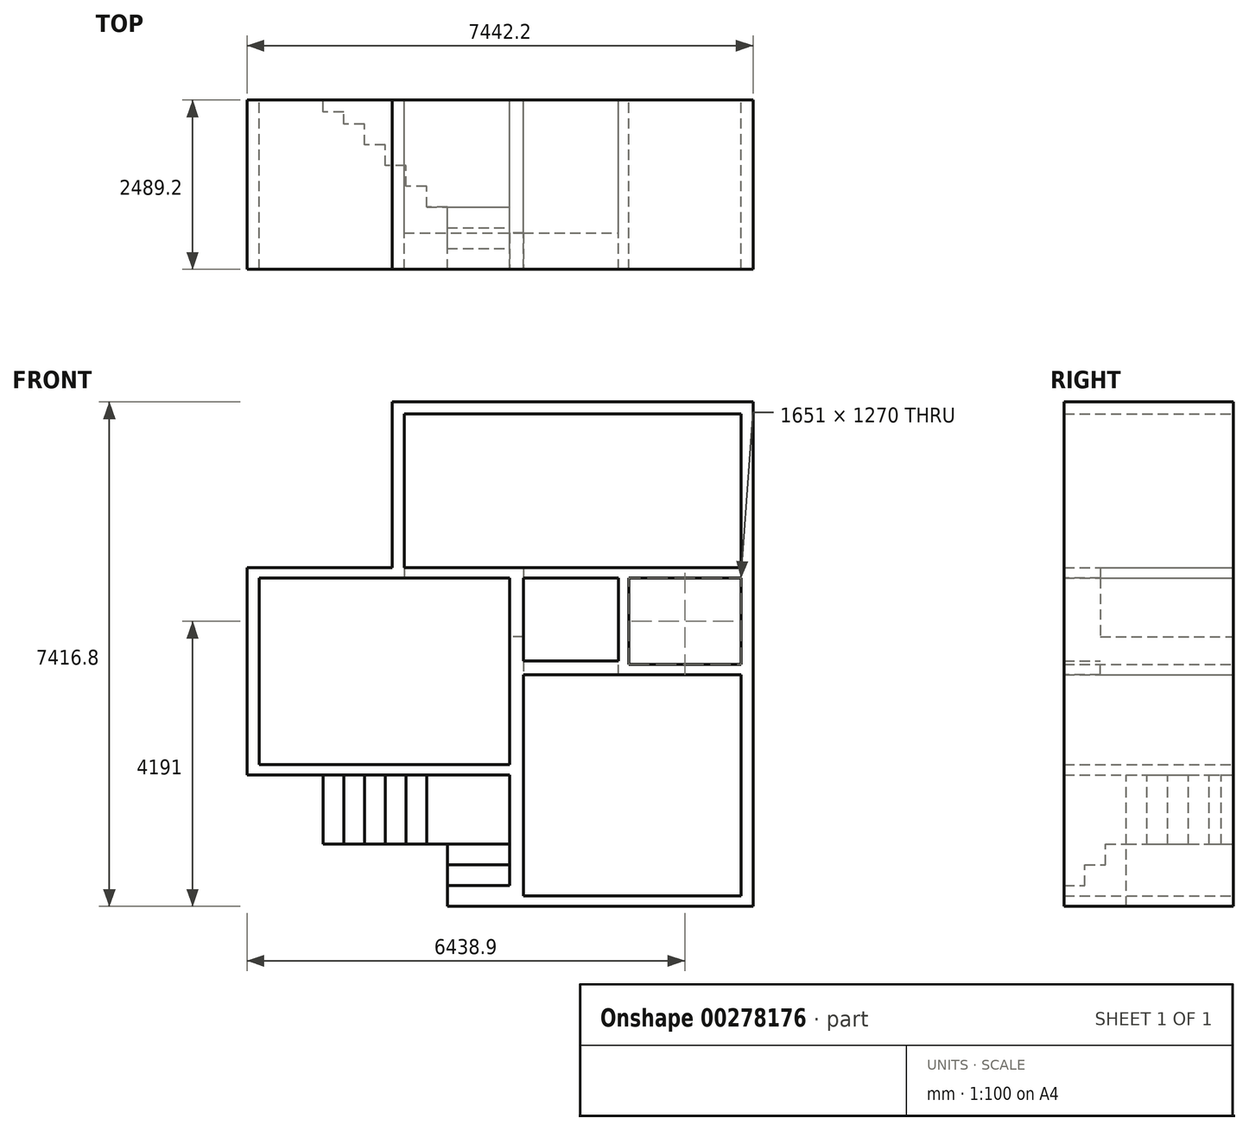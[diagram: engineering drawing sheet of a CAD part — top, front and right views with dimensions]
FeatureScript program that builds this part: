
annotation { "Feature Type Name" : "Feature", "Feature Type Description" : "" }
export const myFeature = defineFeature(function(context is Context, id is Id, definition is map)
    precondition{}
    {
        {
            var Q0;
            Q0=qCreatedBy(makeId("Front.planeOp"),FACE);
            var sketch = newSketch(context, id + "F0", { "sketchPlane" : qUnion([Q0])});
            skLineSegment(sketch, "E0", {"start": v(4953, 0) * mm, "end": v(4953, 2260.6) * mm});
            skLineSegment(sketch, "E1", {"start": v(4953, 2260.6) * mm, "end": v(0, 2260.6) * mm});
            skLineSegment(sketch, "E2", {"start": v(0, 2260.6) * mm, "end": v(0, 0) * mm});
            skLineSegment(sketch, "E3", {"start": v(4953, -1574.8) * mm, "end": v(3149.6, -1574.8) * mm});
            skLineSegment(sketch, "E4", {"start": v(3149.6, -1574.8) * mm, "end": v(3149.6, -152.4) * mm});
            skLineSegment(sketch, "E5", {"start": v(3302, -152.4) * mm, "end": v(3302, -1422.4) * mm});
            skLineSegment(sketch, "E6", {"start": v(3302, -1422.4) * mm, "end": v(4953, -1422.4) * mm});
            skLineSegment(sketch, "E7", {"start": v(4953, -1422.4) * mm, "end": v(4953, -152.4) * mm});
            skLineSegment(sketch, "E8", {"start": v(3302, -152.4) * mm, "end": v(4953, -152.4) * mm});
            skLineSegment(sketch, "E9", {"start": v(5130.8, 2438.4) * mm, "end": v(-177.8, 2438.4) * mm});
            skLineSegment(sketch, "E10", {"start": v(-177.8, 2438.4) * mm, "end": v(-177.8, 0) * mm});
            skLineSegment(sketch, "E11", {"start": v(-177.8, 0) * mm, "end": v(-2311.4, 0) * mm});
            skLineSegment(sketch, "E12", {"start": v(5130.8, 2438.4) * mm, "end": v(5130.8, -4978.4) * mm});
            skLineSegment(sketch, "E13", {"start": v(-2133.6, -152.4) * mm, "end": v(-2133.6, -2895.6) * mm});
            skLineSegment(sketch, "E14", {"start": v(-2133.6, -2895.6) * mm, "end": v(1549.4, -2895.6) * mm});
            skLineSegment(sketch, "E15", {"start": v(-2311.4, -3048) * mm, "end": v(1549.4, -3048) * mm});
            skLineSegment(sketch, "E16", {"start": v(1549.4, -3048) * mm, "end": v(1549.4, -4978.4) * mm});
            skLineSegment(sketch, "E17", {"start": v(1752.6, -4826) * mm, "end": v(4978.4, -4826) * mm});
            skLineSegment(sketch, "E18", {"start": v(1549.4, -4978.4) * mm, "end": v(5130.8, -4978.4) * mm});
            skLineSegment(sketch, "E19", {"start": v(4953, -4826) * mm, "end": v(4953, -1574.8) * mm});
            skLineSegment(sketch, "E20", {"start": v(1752.6, -1016) * mm, "end": v(1752.6, -4826) * mm});
            skLineSegment(sketch, "E21", {"start": v(-2133.6, -152.4) * mm, "end": v(0, -152.4) * mm});
            skLineSegment(sketch, "E22", {"start": v(0, -152.4) * mm, "end": v(0, 0) * mm});
            skLineSegment(sketch, "E23", {"start": v(1549.4, -2895.6) * mm, "end": v(1549.4, -1016) * mm});
            skLineSegment(sketch, "E24", {"start": v(1549.4, -1016) * mm, "end": v(1752.6, -1016) * mm});
            skLineSegment(sketch, "E25", {"start": v(3149.6, -152.4) * mm, "end": v(1752.6, -152.4) * mm});
            skLineSegment(sketch, "E26", {"start": v(1752.6, -152.4) * mm, "end": v(1752.6, 0) * mm});
            skLineSegment(sketch, "E27", {"start": v(1752.6, 0) * mm, "end": v(4953, 0) * mm});
            skLineSegment(sketch, "E28", {"start": v(-2311.4, -3048) * mm, "end": v(-2311.4, 0) * mm});
            skSolve(sketch);
        }
        {
            var Q0;
            Q0 = qSketchRegion(id + "F0", true);
            extrude(context, id + "F1", {"entities" : qUnion([Q0]), "depth" : 2489.2 * mm});
        }
        {
            var Q0;
            Q0=makeQuery(id+"F1.opExtrude","SWEPT_FACE",FACE,{"disambiguationData":[OSD([sQuery(id+"F0.wireOp",EDGE,"E26")])]});
            var sketch = newSketch(context, id + "F2", { "sketchPlane" : qUnion([Q0])});
            skLineSegment(sketch, "E29.bottom", {"start": v(2489.2, 0) * mm, "end": v(1955.8, 0) * mm});
            skLineSegment(sketch, "E29.top", {"start": v(2489.2, -152.4) * mm, "end": v(1955.8, -152.4) * mm});
            skLineSegment(sketch, "E29.left", {"start": v(2489.2, 0) * mm, "end": v(2489.2, -152.4) * mm});
            skLineSegment(sketch, "E29.right", {"start": v(1955.8, 0) * mm, "end": v(1955.8, -152.4) * mm});
            skSolve(sketch);
        }
        {
            var Q0;
            Q0 = qSketchRegion(id + "F2", true);
            var Q1;
            Q1=makeQuery(id+"F1.opExtrude","SWEPT_FACE",FACE,{"disambiguationData":[OSD([sQuery(id+"F0.wireOp",EDGE,"E2"),sQuery(id+"F0.wireOp",EDGE,"E22")])]});
            extrude(context, id + "F3", {"entities" : qUnion([Q0]), "operationType" : NewBodyOperationType.ADD, "endBound" : BoundingType.UP_TO_SURFACE, "endBoundEntityFace" : qUnion([Q1]), "depth" : 25.4 * mm});
        }
        {
            var Q0;
            Q0=makeQuery(id+"F1.opExtrude","SWEPT_FACE",FACE,{"disambiguationData":[OSD([sQuery(id+"F0.wireOp",EDGE,"E24")])]});
            var sketch = newSketch(context, id + "F4", { "sketchPlane" : qUnion([Q0])});
            skLineSegment(sketch, "E30.bottom", {"start": v(1752.6, -2489.2) * mm, "end": v(1549.4, -2489.2) * mm});
            skLineSegment(sketch, "E30.top", {"start": v(1752.6, -1955.8) * mm, "end": v(1549.4, -1955.8) * mm});
            skLineSegment(sketch, "E30.left", {"start": v(1752.6, -2489.2) * mm, "end": v(1752.6, -1955.8) * mm});
            skLineSegment(sketch, "E30.right", {"start": v(1549.4, -2489.2) * mm, "end": v(1549.4, -1955.8) * mm});
            skSolve(sketch);
        }
        {
            var Q0;
            Q0 = qSketchRegion(id + "F4", true);
            var Q1;
            Q1=makeQuery(id+"F3.boolean.opBoolean","MERGE",FACE,{"derivedFrom":[makeQuery(id+"F1.opExtrude","SWEPT_FACE",FACE,{"disambiguationData":[OSD([sQuery(id+"F0.wireOp",EDGE,"E21")])]}),makeQuery(id+"F1.opExtrude","SWEPT_FACE",FACE,{"disambiguationData":[OSD([sQuery(id+"F0.wireOp",EDGE,"E25")])]}),makeQuery(id+"F3.opExtrude","SWEPT_FACE",FACE,{"disambiguationData":[OSD([sQuery(id+"F2.wireOp",EDGE,"E29.top")])]})]});
            extrude(context, id + "F5", {"entities" : qUnion([Q0]), "operationType" : NewBodyOperationType.ADD, "endBound" : BoundingType.UP_TO_SURFACE, "endBoundEntityFace" : qUnion([Q1]), "depth" : 25.4 * mm});
        }
        {
            var Q0;
            Q0=makeQuery(id+"F1.opExtrude","SWEPT_FACE",FACE,{"disambiguationData":[OSD([sQuery(id+"F0.wireOp",EDGE,"E4")])]});
            var sketch = newSketch(context, id + "F6", { "sketchPlane" : qUnion([Q0])});
            skLineSegment(sketch, "E31.bottom", {"start": v(2489.2, -1574.8) * mm, "end": v(1955.8, -1574.8) * mm});
            skLineSegment(sketch, "E31.top", {"start": v(2489.2, -1371.6) * mm, "end": v(1955.8, -1371.6) * mm});
            skLineSegment(sketch, "E31.left", {"start": v(2489.2, -1574.8) * mm, "end": v(2489.2, -1371.6) * mm});
            skLineSegment(sketch, "E31.right", {"start": v(1955.8, -1574.8) * mm, "end": v(1955.8, -1371.6) * mm});
            skSolve(sketch);
        }
        {
            var Q0;
            Q0 = qSketchRegion(id + "F6", true);
            var Q1;
            Q1=makeQuery(id+"F5.boolean.opBoolean","MERGE",FACE,{"derivedFrom":[makeQuery(id+"F1.opExtrude","SWEPT_FACE",FACE,{"disambiguationData":[OSD([sQuery(id+"F0.wireOp",EDGE,"E20")])]}),makeQuery(id+"F5.opExtrude","SWEPT_FACE",FACE,{"disambiguationData":[OSD([sQuery(id+"F4.wireOp",EDGE,"E30.left")])]})]});
            extrude(context, id + "F7", {"entities" : qUnion([Q0]), "operationType" : NewBodyOperationType.ADD, "endBound" : BoundingType.UP_TO_SURFACE, "endBoundEntityFace" : qUnion([Q1]), "depth" : 25.4 * mm});
        }
        {
            var Q0;
            Q0=makeQuery(id+"F1.opExtrude","SWEPT_FACE",FACE,{"disambiguationData":[OSD([sQuery(id+"F0.wireOp",EDGE,"E16")])]});
            var sketch = newSketch(context, id + "F8", { "sketchPlane" : qUnion([Q0])});
            skLineSegment(sketch, "E32", {"start": v(2489.2, -4978.4) * mm, "end": v(2489.2, -4673.6) * mm});
            skLineSegment(sketch, "E33", {"start": v(2489.2, -4673.6) * mm, "end": v(2184.4, -4673.6) * mm});
            skLineSegment(sketch, "E34", {"start": v(2184.4, -4673.6) * mm, "end": v(2184.4, -4368.8) * mm});
            skLineSegment(sketch, "E35", {"start": v(2184.4, -4368.8) * mm, "end": v(1879.6, -4368.8) * mm});
            skLineSegment(sketch, "E36", {"start": v(1879.6, -4368.8) * mm, "end": v(1879.6, -4064) * mm});
            skLineSegment(sketch, "E37", {"start": v(1879.6, -4064) * mm, "end": v(1574.8, -4064) * mm});
            skLineSegment(sketch, "E38", {"start": v(1244.6, -4978.4) * mm, "end": v(2489.2, -4978.4) * mm});
            skLineSegment(sketch, "E39", {"start": v(1574.8, -4064) * mm, "end": v(1574.8, -3759.2) * mm});
            skLineSegment(sketch, "E40", {"start": v(1574.8, -3759.2) * mm, "end": v(1270, -3759.2) * mm});
            skLineSegment(sketch, "E41", {"start": v(1270, -3759.2) * mm, "end": v(1270, -4978.4) * mm});
            skSolve(sketch);
        }
        {
            var Q0;
            Q0=makeQuery(id+"F8.imprint","IMPRINT",FACE,{"disambiguationData":[TD([[makeQuery(id+"F8.imprint","IMPRINT",EDGE,{"derivedFrom":sQuery(id+"F8.wireOp",EDGE,"E32")}),-1.0]])]});
            extrude(context, id + "F9", {"entities" : qUnion([Q0]), "operationType" : NewBodyOperationType.ADD, "depth" : 914.4 * mm, "offsetDistance" : 25.4 * mm});
        }
        {
            var Q0;
            Q0=makeQuery(id+"F9.opExtrude","SWEPT_FACE",FACE,{"disambiguationData":[OSD([sQuery(id+"F8.wireOp",EDGE,"E40")])]});
            extrude(context, id + "F10", {"entities" : qUnion([Q0]), "operationType" : NewBodyOperationType.ADD, "endBound" : BoundingType.UP_TO_NEXT, "depth" : 25.4 * mm, "offsetDistance" : 25.4 * mm});
        }
        {
            var Q0;
            {var subQ0=sQuery(id+"F8.wireOp",EDGE,"E41");Q0=makeQuery(id+"F10.boolean.opBoolean","MERGE",FACE,{"derivedFrom":[makeQuery(id+"F9.opExtrude","SWEPT_FACE",FACE,{"disambiguationData":[OSD([subQ0])]}),makeQuery(id+"F10.opExtrude","SWEPT_FACE",FACE,{"disambiguationData":[OSD([sQuery(id+"F8.wireOp",EDGE,"E40"),subQ0])]})]});}
            var Q1;
            Q1=makeQuery(id+"F1.opExtrude","CAP_FACE",FACE,{"disambiguationData":[OSD([sQuery(id+"F0.wireOp",EDGE,"E0"),sQuery(id+"F0.wireOp",EDGE,"E1"),sQuery(id+"F0.wireOp",EDGE,"E2"),sQuery(id+"F0.wireOp",EDGE,"E3"),sQuery(id+"F0.wireOp",EDGE,"E4"),sQuery(id+"F0.wireOp",EDGE,"E5"),sQuery(id+"F0.wireOp",EDGE,"E6"),sQuery(id+"F0.wireOp",EDGE,"E7"),sQuery(id+"F0.wireOp",EDGE,"E8"),sQuery(id+"F0.wireOp",EDGE,"E9"),sQuery(id+"F0.wireOp",EDGE,"E10"),sQuery(id+"F0.wireOp",EDGE,"E11"),sQuery(id+"F0.wireOp",EDGE,"E12"),sQuery(id+"F0.wireOp",EDGE,"E13"),sQuery(id+"F0.wireOp",EDGE,"E14"),sQuery(id+"F0.wireOp",EDGE,"E15"),sQuery(id+"F0.wireOp",EDGE,"E16"),sQuery(id+"F0.wireOp",EDGE,"E17"),sQuery(id+"F0.wireOp",EDGE,"E18"),sQuery(id+"F0.wireOp",EDGE,"E19"),sQuery(id+"F0.wireOp",EDGE,"E20"),sQuery(id+"F0.wireOp",EDGE,"E21"),sQuery(id+"F0.wireOp",EDGE,"E22"),sQuery(id+"F0.wireOp",EDGE,"E23"),sQuery(id+"F0.wireOp",EDGE,"E24"),sQuery(id+"F0.wireOp",EDGE,"E25"),sQuery(id+"F0.wireOp",EDGE,"E26"),sQuery(id+"F0.wireOp",EDGE,"E27"),sQuery(id+"F0.wireOp",EDGE,"E28")])],"isStart":true});
            extrude(context, id + "F11", {"entities" : qUnion([Q0]), "operationType" : NewBodyOperationType.ADD, "endBound" : BoundingType.UP_TO_SURFACE, "depth" : 25.4 * mm, "endBoundEntityFace" : qUnion([Q1]), "offsetDistance" : 25.4 * mm});
        }
        {
            var Q0;
            Q0=makeQuery(id+"F1.opExtrude","SWEPT_FACE",FACE,{"disambiguationData":[OSD([sQuery(id+"F0.wireOp",EDGE,"E15")])]});
            var sketch = newSketch(context, id + "F12", { "sketchPlane" : qUnion([Q0])});
            skLineSegment(sketch, "E42", {"start": v(635, 1574.8) * mm, "end": v(330.2, 1574.8) * mm});
            skLineSegment(sketch, "E43", {"start": v(330.2, 1574.8) * mm, "end": v(330.2, 1270) * mm});
            skLineSegment(sketch, "E44", {"start": v(330.2, 1270) * mm, "end": v(25.4, 1270) * mm});
            skLineSegment(sketch, "E45", {"start": v(25.4, 1270) * mm, "end": v(25.4, 965.2) * mm});
            skLineSegment(sketch, "E46", {"start": v(25.4, 965.2) * mm, "end": v(-279.4, 965.2) * mm});
            skLineSegment(sketch, "E47", {"start": v(-279.4, 965.2) * mm, "end": v(-279.4, 660.4) * mm});
            skLineSegment(sketch, "E48", {"start": v(-279.4, 660.4) * mm, "end": v(-584.2, 660.4) * mm});
            skLineSegment(sketch, "E49", {"start": v(-584.2, 660.4) * mm, "end": v(-584.2, 355.6) * mm});
            skLineSegment(sketch, "E50", {"start": v(-584.2, 355.6) * mm, "end": v(-889, 355.6) * mm});
            skLineSegment(sketch, "E51", {"start": v(-889, 355.6) * mm, "end": v(-889, 176.38) * mm});
            skLineSegment(sketch, "E52", {"start": v(-889, 176.38) * mm, "end": v(-1193.8, 176.38) * mm});
            skLineSegment(sketch, "E53", {"start": v(-1193.8, 176.38) * mm, "end": v(-1193.8, 0) * mm});
            skLineSegment(sketch, "E54", {"start": v(-1193.8, 0) * mm, "end": v(635, 0) * mm});
            skLineSegment(sketch, "E55", {"start": v(635, 0) * mm, "end": v(635, 1574.8) * mm});
            skSolve(sketch);
        }
        {
            var Q0;
            Q0 = qSketchRegion(id + "F12", true);
            var Q1;
            Q1=makeQuery(id+"F9.opExtrude","SWEPT_FACE",FACE,{"disambiguationData":[OSD([sQuery(id+"F8.wireOp",EDGE,"E37")])]});
            extrude(context, id + "F13", {"entities" : qUnion([Q0]), "operationType" : NewBodyOperationType.ADD, "endBound" : BoundingType.UP_TO_SURFACE, "depth" : 25.4 * mm, "endBoundEntityFace" : qUnion([Q1]), "offsetDistance" : 25.4 * mm});
        }
        {
            var Q0;
            {var subQ0=sQuery(id+"F0.wireOp",EDGE,"E28");var subQ1=sQuery(id+"F0.wireOp",EDGE,"E27");var subQ2=sQuery(id+"F0.wireOp",EDGE,"E26");var subQ3=sQuery(id+"F0.wireOp",EDGE,"E25");var subQ4=sQuery(id+"F0.wireOp",EDGE,"E24");var subQ5=sQuery(id+"F0.wireOp",EDGE,"E23");var subQ6=sQuery(id+"F0.wireOp",EDGE,"E22");var subQ7=sQuery(id+"F0.wireOp",EDGE,"E21");var subQ8=sQuery(id+"F0.wireOp",EDGE,"E20");var subQ9=sQuery(id+"F0.wireOp",EDGE,"E19");var subQ10=sQuery(id+"F0.wireOp",EDGE,"E18");var subQ11=sQuery(id+"F0.wireOp",EDGE,"E17");var subQ12=sQuery(id+"F0.wireOp",EDGE,"E16");var subQ13=sQuery(id+"F0.wireOp",EDGE,"E15");var subQ14=sQuery(id+"F0.wireOp",EDGE,"E14");var subQ15=sQuery(id+"F0.wireOp",EDGE,"E13");var subQ16=sQuery(id+"F0.wireOp",EDGE,"E12");var subQ17=sQuery(id+"F0.wireOp",EDGE,"E11");var subQ18=sQuery(id+"F0.wireOp",EDGE,"E10");var subQ19=sQuery(id+"F0.wireOp",EDGE,"E9");var subQ20=sQuery(id+"F0.wireOp",EDGE,"E8");var subQ21=sQuery(id+"F0.wireOp",EDGE,"E7");var subQ22=sQuery(id+"F0.wireOp",EDGE,"E6");var subQ23=sQuery(id+"F0.wireOp",EDGE,"E5");var subQ24=sQuery(id+"F0.wireOp",EDGE,"E4");var subQ25=sQuery(id+"F0.wireOp",EDGE,"E3");var subQ26=sQuery(id+"F0.wireOp",EDGE,"E2");var subQ27=sQuery(id+"F0.wireOp",EDGE,"E1");var subQ28=sQuery(id+"F0.wireOp",EDGE,"E0");Q0=makeQuery(id+"F13.boolean.opBoolean","MERGE",FACE,{"derivedFrom":[makeQuery(id+"F11.boolean.opBoolean","MERGE",FACE,{"derivedFrom":[makeQuery(id+"F1.opExtrude","CAP_FACE",FACE,{"disambiguationData":[OSD([subQ28,subQ27,subQ26,subQ25,subQ24,subQ23,subQ22,subQ21,subQ20,subQ19,subQ18,subQ17,subQ16,subQ15,subQ14,subQ13,subQ12,subQ11,subQ10,subQ9,subQ8,subQ7,subQ6,subQ5,subQ4,subQ3,subQ2,subQ1,subQ0])],"isStart":true}),makeQuery(id+"F11.opExtrude","CAP_FACE",FACE,{"disambiguationData":[OSD([subQ28,subQ27,subQ26,subQ25,subQ24,subQ23,subQ22,subQ21,subQ20,subQ19,subQ18,subQ17,subQ16,subQ15,subQ14,subQ13,subQ12,subQ11,subQ10,subQ9,subQ8,subQ7,subQ6,subQ5,subQ4,subQ3,subQ2,subQ1,subQ0])],"isStart":false})]}),makeQuery(id+"F13.opExtrude","SWEPT_FACE",FACE,{"disambiguationData":[OSD([sQuery(id+"F12.wireOp",EDGE,"E54")])]})]});}
            var sketch = newSketch(context, id + "F14", { "sketchPlane" : qUnion([Q0])});
            skLineSegment(sketch, "E56", {"start": v(-1549.4, -4978.4) * mm, "end": v(-1549.4, -4064) * mm});
            skLineSegment(sketch, "E57", {"start": v(-1549.4, -4064) * mm, "end": v(-635, -4064) * mm});
            skLineSegment(sketch, "E58", {"start": v(-635, -4064) * mm, "end": v(-635, -4978.4) * mm});
            skLineSegment(sketch, "E59", {"start": v(-635, -4978.4) * mm, "end": v(-1549.4, -4978.4) * mm});
            skSolve(sketch);
        }
        {
            var Q0;
            Q0 = qSketchRegion(id + "F14", true);
            extrude(context, id + "F15", {"entities" : qUnion([Q0]), "operationType" : NewBodyOperationType.REMOVE, "oppositeDirection" : true, "depth" : 1574.55 * mm, "offsetDistance" : 25.4 * mm});
        }
    });
